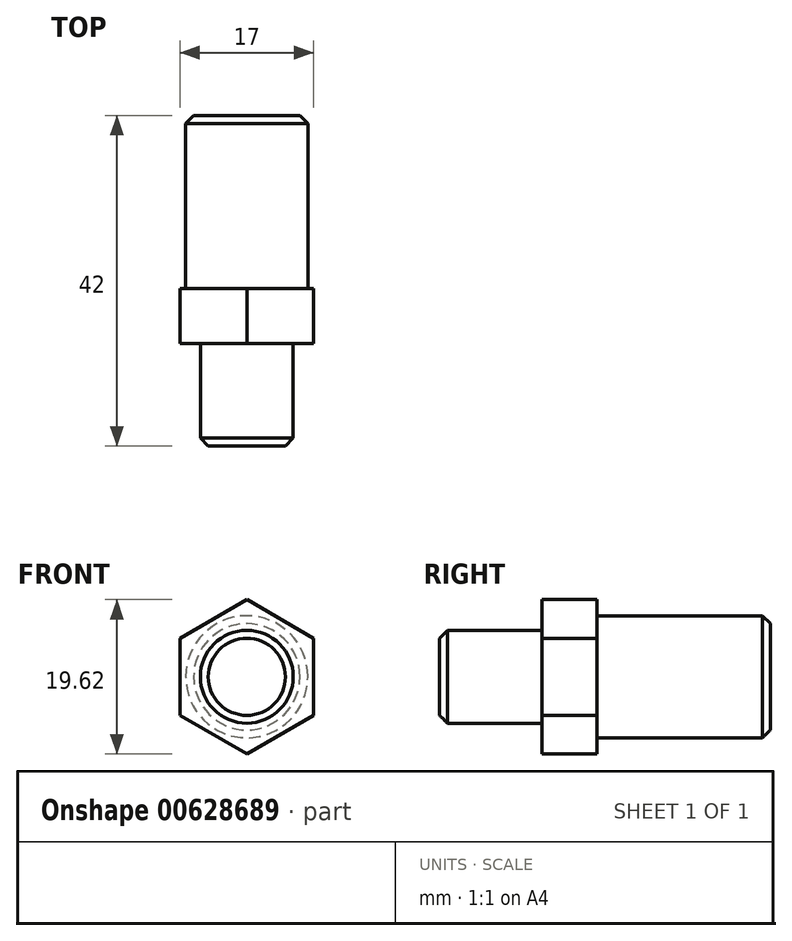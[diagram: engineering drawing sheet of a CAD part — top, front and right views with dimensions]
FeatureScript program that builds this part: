
annotation { "Feature Type Name" : "Feature", "Feature Type Description" : "" }
export const myFeature = defineFeature(function(context is Context, id is Id, definition is map)
    precondition{}
    {
        {
            var Q0;
            Q0=qCreatedBy(makeId("Front.planeOp"),FACE);
            var sketch = newSketch(context, id + "F0", { "sketchPlane" : qUnion([Q0])});
            skCircle(sketch, "E0", {"center": v(0, 0) * mm, "radius": 7.75 * mm});
            skSolve(sketch);
        }
        {
            var Q0;
            Q0 = qSketchRegion(id + "F0", true);
            extrude(context, id + "F1", {"entities" : qUnion([Q0]), "depth" : 22 * mm, "offsetDistance" : 25 * mm});
        }
        {
            var Q0;
            Q0=makeQuery(id+"F1.opExtrude","CAP_FACE",FACE,{"disambiguationData":[OSD([sQuery(id+"F0.wireOp",EDGE,"E0")])],"isStart":false});
            var sketch = newSketch(context, id + "F2", { "sketchPlane" : qUnion([Q0])});
            skCircle(sketch, "E1.cCircle", {"center": v(0, 0) * mm, "radius": 8.5 * mm, "construction": true});
            skLineSegment(sketch, "E1.0", {"start": v(8.5, 4.9) * mm, "end": v(8.5, -4.9) * mm});
            skLineSegment(sketch, "E1.1", {"start": v(8.5, -4.9) * mm, "end": v(0, -9.81) * mm});
            skLineSegment(sketch, "E1.2", {"start": v(0, -9.81) * mm, "end": v(-8.5, -4.9) * mm});
            skLineSegment(sketch, "E1.3", {"start": v(-8.5, -4.9) * mm, "end": v(-8.5, 4.9) * mm});
            skLineSegment(sketch, "E1.4", {"start": v(-8.5, 4.9) * mm, "end": v(0, 9.81) * mm});
            skLineSegment(sketch, "E1.5", {"start": v(0, 9.81) * mm, "end": v(8.5, 4.9) * mm});
            skPoint(sketch, "E1.0.midPoint", {"position": v(8.5, 0) * mm});
            skSolve(sketch);
        }
        {
            var Q0;
            Q0 = qSketchRegion(id + "F2", true);
            extrude(context, id + "F3", {"entities" : qUnion([Q0]), "operationType" : NewBodyOperationType.ADD, "depth" : 7 * mm, "offsetDistance" : 25 * mm});
        }
        {
            var Q0;
            Q0=makeQuery(id+"F3.opExtrude","CAP_FACE",FACE,{"disambiguationData":[OSD([sQuery(id+"F2.wireOp",EDGE,"E1.0"),sQuery(id+"F2.wireOp",EDGE,"E1.1"),sQuery(id+"F2.wireOp",EDGE,"E1.2"),sQuery(id+"F2.wireOp",EDGE,"E1.3"),sQuery(id+"F2.wireOp",EDGE,"E1.4"),sQuery(id+"F2.wireOp",EDGE,"E1.5")])],"isStart":false});
            var sketch = newSketch(context, id + "F4", { "sketchPlane" : qUnion([Q0])});
            skCircle(sketch, "E2", {"center": v(0, 0) * mm, "radius": 5.9 * mm});
            skSolve(sketch);
        }
        {
            var Q0;
            Q0 = qSketchRegion(id + "F4", true);
            extrude(context, id + "F5", {"entities" : qUnion([Q0]), "operationType" : NewBodyOperationType.ADD, "depth" : 13 * mm, "offsetDistance" : 25 * mm});
        }
        {
            var Q0;
            Q0=makeQuery(id+"F5.opExtrude","CAP_EDGE",EDGE,{"disambiguationData":[OSD([sQuery(id+"F4.wireOp",EDGE,"E2")])],"isStart":false});
            var Q1;
            Q1=makeQuery(id+"F1.opExtrude","CAP_EDGE",EDGE,{"disambiguationData":[OSD([sQuery(id+"F0.wireOp",EDGE,"E0")])],"isStart":true});
            chamfer(context, id + "F6", {"entities" : qUnion([Q0, Q1]), "width" : 1 * mm, "tangentPropagation" : true});
        }
    });
